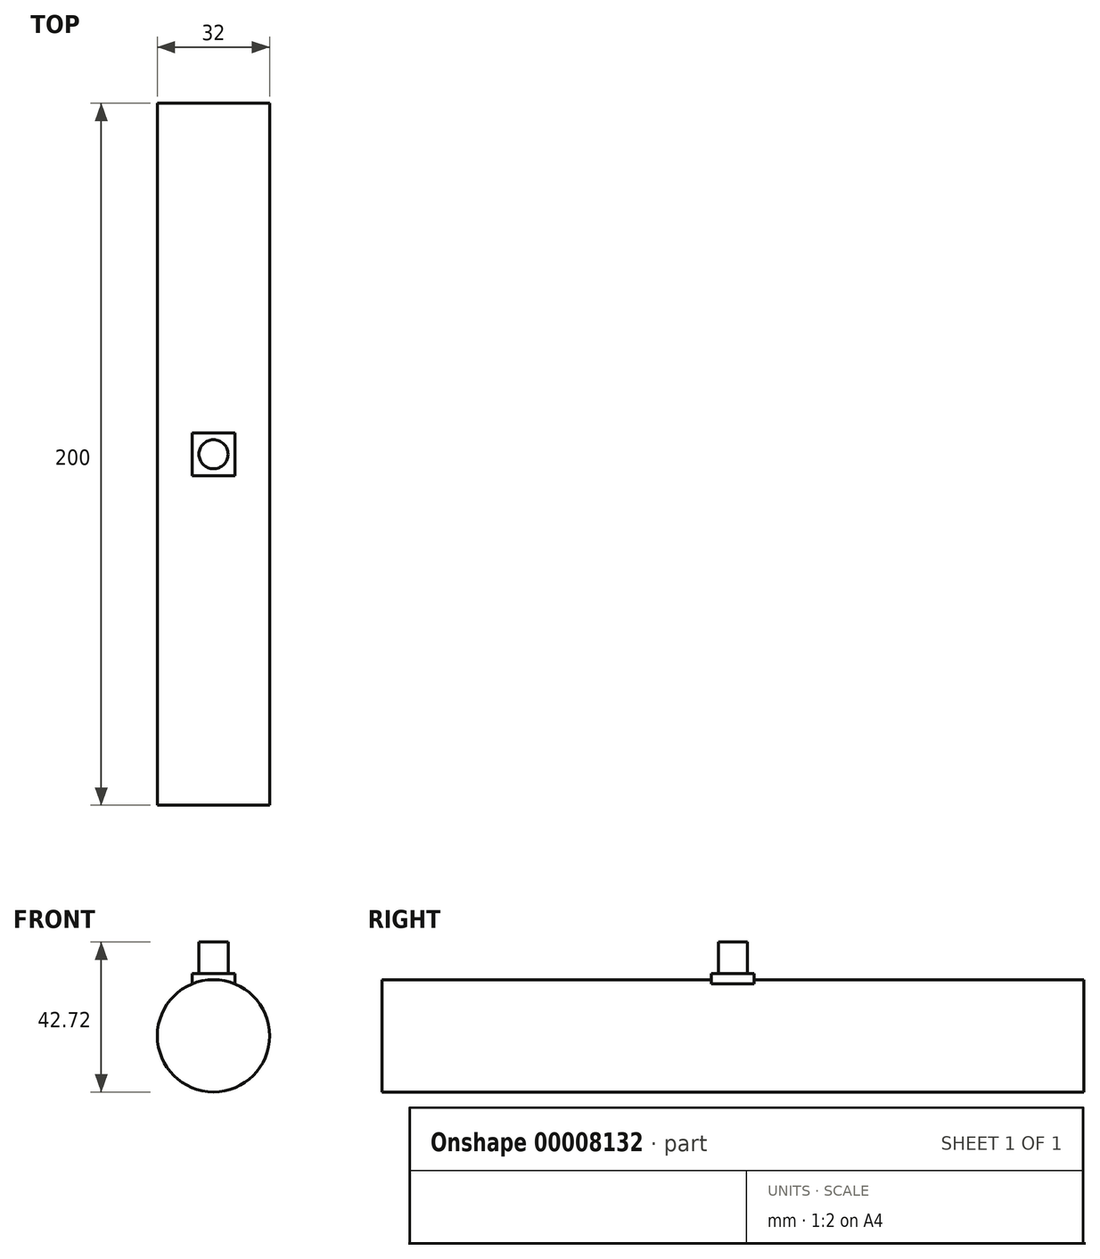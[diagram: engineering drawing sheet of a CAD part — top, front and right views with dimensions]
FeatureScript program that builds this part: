
annotation { "Feature Type Name" : "Feature", "Feature Type Description" : "" }
export const myFeature = defineFeature(function(context is Context, id is Id, definition is map)
    precondition{}
    {
        {
            var Q0;
            Q0=qCreatedBy(makeId("Front.planeOp"),FACE);
            var sketch = newSketch(context, id + "F0", { "sketchPlane" : qUnion([Q0])});
            skCircle(sketch, "E0", {"center": v(0, 0) * mm, "radius": 16 * mm});
            skSolve(sketch);
        }
        {
            var Q0;
            Q0 = qSketchRegion(id + "F0", true);
            extrude(context, id + "F1", {"entities" : qUnion([Q0]), "endBound" : BoundingType.SYMMETRIC, "depth" : 200 * mm});
        }
        {
            var Q0;
            Q0=qCreatedBy(makeId("Top.planeOp"),FACE);
            var sketch = newSketch(context, id + "F2", { "sketchPlane" : qUnion([Q0])});
            skLineSegment(sketch, "E1.rect.bottom", {"start": v(6.1, 6.1) * mm, "end": v(-6.1, 6.1) * mm});
            skLineSegment(sketch, "E1.rect.top", {"start": v(6.1, -6.1) * mm, "end": v(-6.1, -6.1) * mm});
            skLineSegment(sketch, "E1.rect.left", {"start": v(6.1, 6.1) * mm, "end": v(6.1, -6.1) * mm});
            skLineSegment(sketch, "E1.rect.right", {"start": v(-6.1, 6.1) * mm, "end": v(-6.1, -6.1) * mm});
            skPoint(sketch, "E1.rect.middle", {"position": v(0, 0) * mm});
            skSolve(sketch);
        }
        {
            var Q0;
            Q0 = qSketchRegion(id + "F2", true);
            extrude(context, id + "F3", {"entities" : qUnion([Q0]), "operationType" : NewBodyOperationType.ADD, "depth" : 17.8 * mm});
        }
        {
            var Q0;
            Q0=makeQuery(id+"F3.opExtrude","CAP_FACE",FACE,{"disambiguationData":[OSD([sQuery(id+"F2.wireOp",EDGE,"E1.rect.bottom"),sQuery(id+"F2.wireOp",EDGE,"E1.rect.top"),sQuery(id+"F2.wireOp",EDGE,"E1.rect.left"),sQuery(id+"F2.wireOp",EDGE,"E1.rect.right")])],"isStart":false});
            var sketch = newSketch(context, id + "F4", { "sketchPlane" : qUnion([Q0])});
            skCircle(sketch, "E2", {"center": v(0, 0) * mm, "radius": 4.15 * mm});
            skSolve(sketch);
        }
        {
            var Q0;
            Q0 = qSketchRegion(id + "F4", true);
            extrude(context, id + "F5", {"entities" : qUnion([Q0]), "operationType" : NewBodyOperationType.ADD, "depth" : 8.93 * mm});
        }
    });
